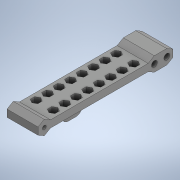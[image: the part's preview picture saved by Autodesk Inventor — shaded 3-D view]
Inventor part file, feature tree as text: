
AUTODESK INVENTOR PART (.ipt)
format: ipt  version: 2020 (Build 240168000, 168)  size: 496,128 bytes
history: native  units: in
note: dims shown in document units (in); Inventor stores cm internally (conversion verified against a paired STEP export)
features: sketch x7, extrude x6, projected_geometry x4, plane x2, mirror x1, fillet x1
ambient origin geometry x8: Origin, YZ Plane, XZ Plane, XY Plane, X Axis, Y Axis, Z Axis, Center Point
bodies: Solid1 (feature_tree)
feature tree (21):
  extrude  "Extrusion1"  Depth=3.4256in
  plane  "Work Plane1"
  extrude  "Extrusion2"  Depth=0.7874in
  sketch  "Sketch4"  dims[d4=0.0in d5=0.0827in]
  extrude  "Extrusion4"  Depth=0.0827in
  plane  "Work Plane2"
  extrude  "Extrusion6"  Depth=3.1106in
  mirror  "Mirror2"
  extrude  "Extrusion7"  Depth=0.315in
  extrude  "Extrusion8"  Depth=0.2362in
  fillet  "Fillet1"  [1 undecoded]
  sketch  "Sketch1"  dims[d0=0.1818in d1=3.4256in]
  sketch  "Sketch2"  dims[d2=0.0984in d3=0.7874in]
  sketch  "Sketch5"  dims[d6=0.7874in d7=0.0in d28=3.1106in]
  sketch  "Sketch7"  dims[d29=0.315in d31=0.315in]
  projected_geometry  "Projected Loop7"
  projected_geometry  "Projected Loop8"
  sketch  "Sketch8"  dims[d33=0.1476in d34=0.2362in d35=0.0in]
  projected_geometry  "Projected Loop9"
  sketch  "Sketch10"  dims[d38=0.315in d39=0.2756in d40=-0.3092in d41=0.0787in d42=0.0787in d43=0.0787in d44=3.1496in d46=0.2913in d47=0.3937in d49=0.3937in d51=3.1496in d53=0.2913in d54=0.3937in d56=0.3937in d58=0.0in d59=0.0in d60=1.0994in d61=0.1378in d63=1.1811in d64=0.1575in d65=0.0in d66=0.126in d67=0.1575in]
  projected_geometry  "Projected Loop10"
note: 1 required parameter value undecoded (feature->parameter linkage not recoverable at this tier; creation-order binding heuristic only, values carry confidence <= 0.55)
